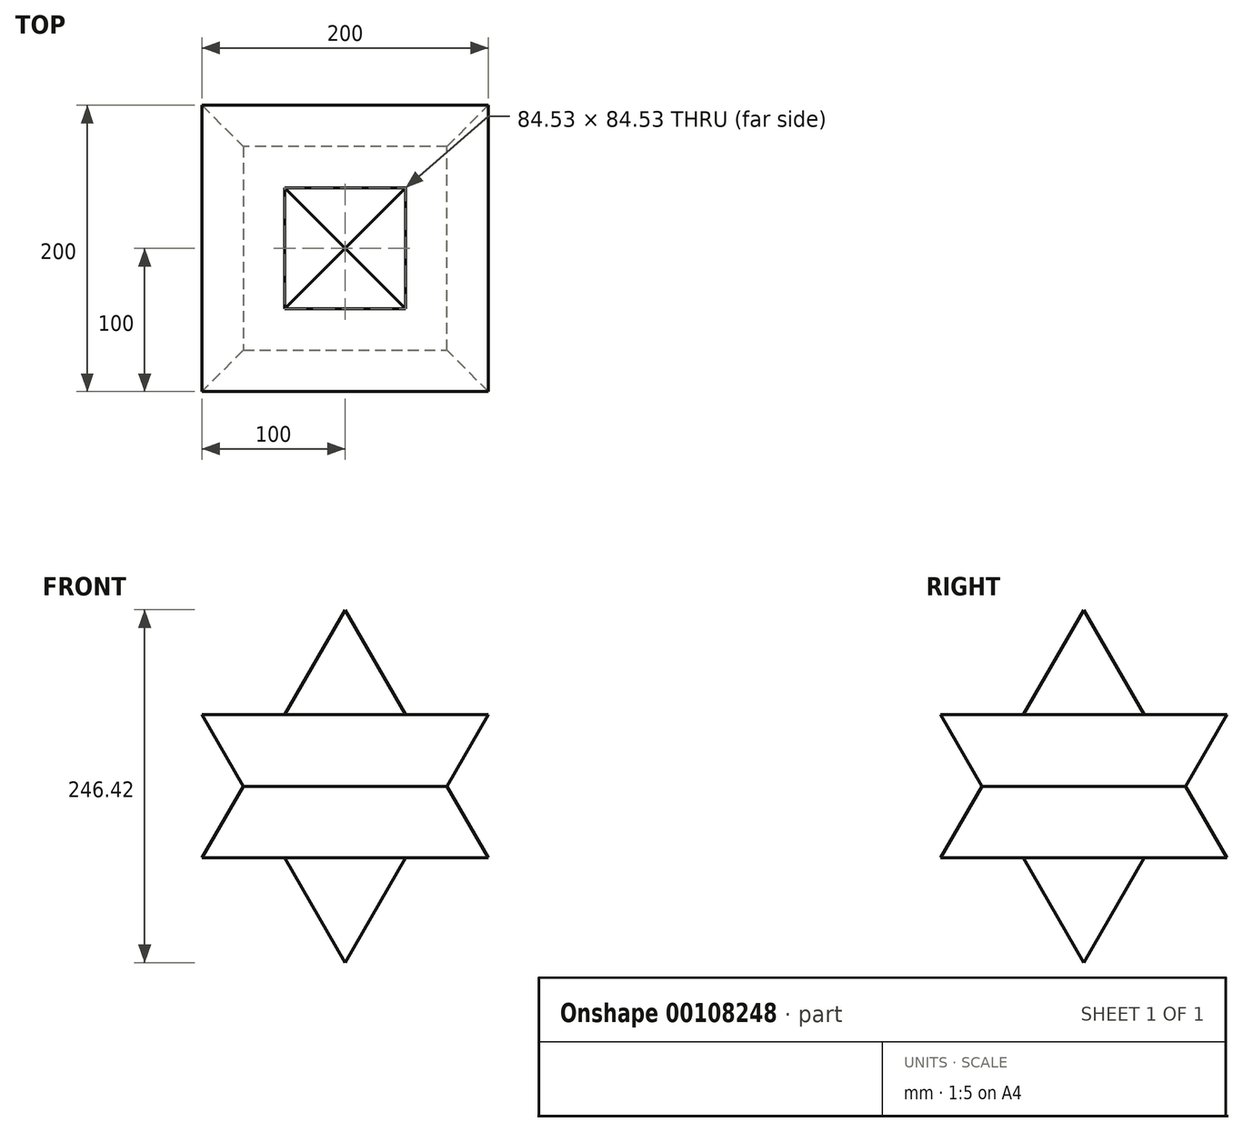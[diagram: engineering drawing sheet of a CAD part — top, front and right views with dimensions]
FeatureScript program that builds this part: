
annotation { "Feature Type Name" : "Feature", "Feature Type Description" : "" }
export const myFeature = defineFeature(function(context is Context, id is Id, definition is map)
    precondition{}
    {
        {
            var Q0;
            Q0=qCreatedBy(makeId("Top.planeOp"),FACE);
            var sketch = newSketch(context, id + "F0", { "sketchPlane" : qUnion([Q0])});
            skLineSegment(sketch, "E0.bottom", {"start": v(-100, 100) * mm, "end": v(100, 100) * mm});
            skLineSegment(sketch, "E0.top", {"start": v(-100, -100) * mm, "end": v(100, -100) * mm});
            skLineSegment(sketch, "E0.left", {"start": v(-100, 100) * mm, "end": v(-100, -100) * mm});
            skLineSegment(sketch, "E0.right", {"start": v(100, 100) * mm, "end": v(100, -100) * mm});
            skPoint(sketch, "E0.middle", {"position": v(0, 0) * mm});
            skSolve(sketch);
        }
        {
            var Q0;
            Q0 = qSketchRegion(id + "F0", true);
            extrude(context, id + "F1", {"entities" : qUnion([Q0]), "depth" : 200 * mm, "hasDraft" : true, "draftAngle" : 30 * degree, "draftPullDirection" : true});
        }
        {
            var Q0;
            Q0=qCreatedBy(makeId("Top.planeOp"),FACE);
            cPlane(context, id + "F2", {"entities" : qUnion([Q0]), "cplaneType" : CPlaneType.OFFSET, "offset" : 100 * mm, "width" : 150 * mm, "height" : 150 * mm});
        }
        {
            var Q0;
            Q0=qCreatedBy(id+"F2.planeOp",FACE);
            var sketch = newSketch(context, id + "F3", { "sketchPlane" : qUnion([Q0])});
            skLineSegment(sketch, "E1.bottom", {"start": v(-100, -100) * mm, "end": v(100, -100) * mm});
            skLineSegment(sketch, "E1.top", {"start": v(-100, 100) * mm, "end": v(100, 100) * mm});
            skLineSegment(sketch, "E1.left", {"start": v(-100, -100) * mm, "end": v(-100, 100) * mm});
            skLineSegment(sketch, "E1.right", {"start": v(100, -100) * mm, "end": v(100, 100) * mm});
            skPoint(sketch, "E1.middle", {"position": v(0, 0) * mm});
            skSolve(sketch);
        }
        {
            var Q0;
            Q0 = qSketchRegion(id + "F3", true);
            extrude(context, id + "F4", {"entities" : qUnion([Q0]), "operationType" : NewBodyOperationType.ADD, "oppositeDirection" : true, "depth" : 200 * mm, "hasDraft" : true, "draftAngle" : 30 * degree, "draftPullDirection" : true});
        }
    });
